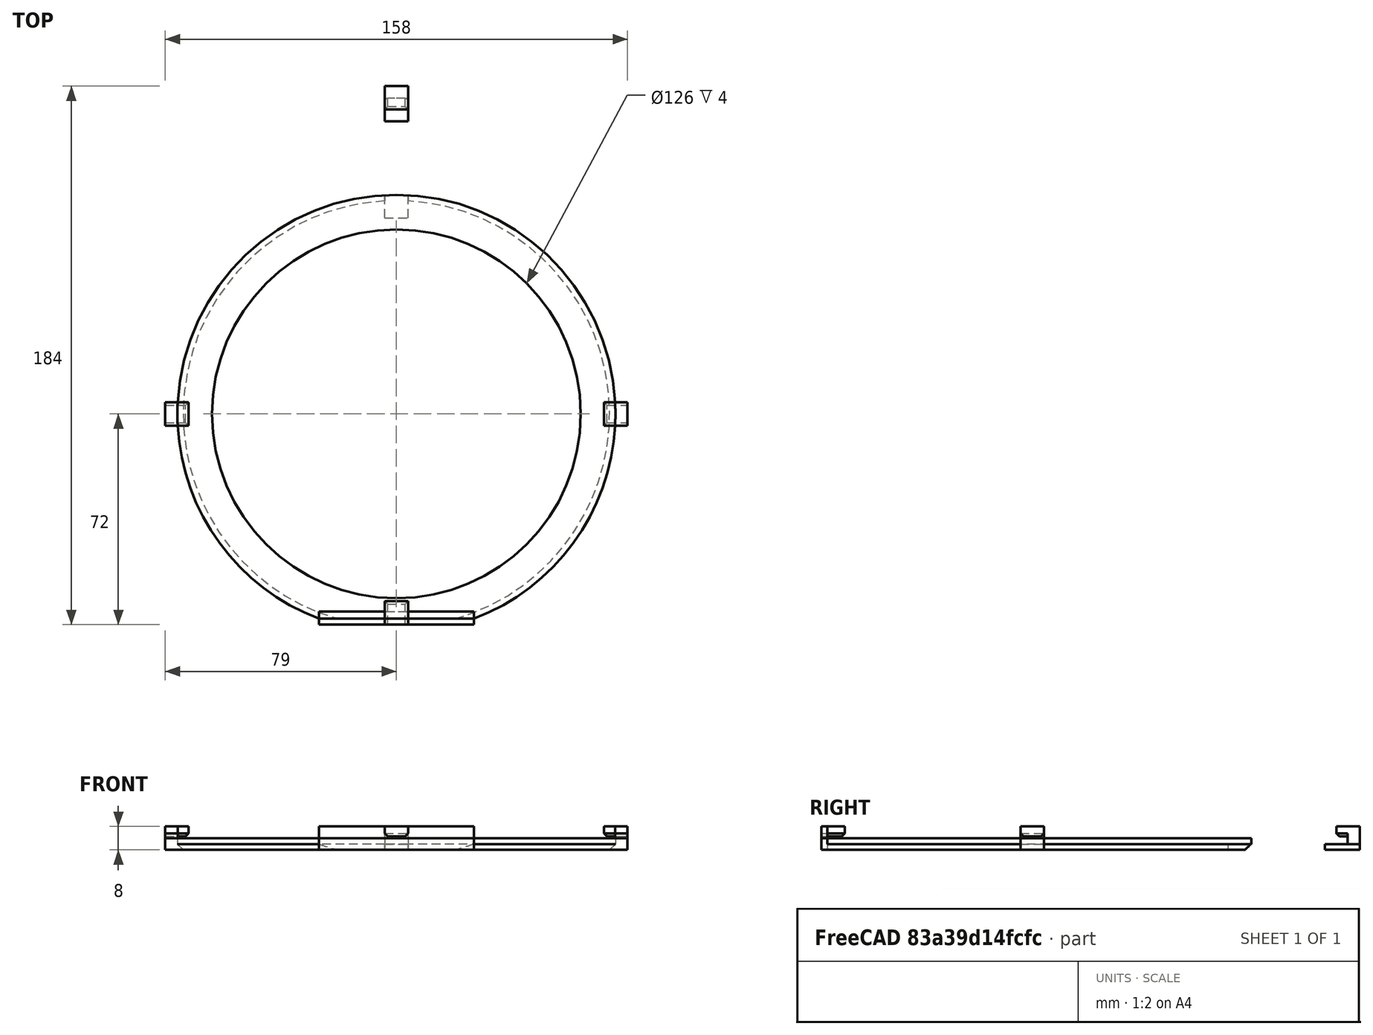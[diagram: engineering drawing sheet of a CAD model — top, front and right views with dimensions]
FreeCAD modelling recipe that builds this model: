
FCSTD DOCUMENT  (FreeCAD 0.19R0.19.2)
Label: waferHolder_009
License: All rights reserved
LicenseURL: http://en.wikipedia.org/wiki/All_rights_reserved
objects: Part::Box×18, Part::Chamfer×14, Part::Cut×8, Sketcher::SketchObject×5, Part::Extrusion×5, Part::MultiFuse×2
note: 52 computed .brp shape members not serialized (recipe doc carries the construction recipe); baked Part::Feature solids carry a one-line shape summary decoded from their .brp

FEATURE [Sketcher::SketchObject] Sketch
  FullyConstrained = true
  sketch-geometry (3):
    g0: Circle CenterX=-3.1415e-12 CenterY=5.6243e-12 CenterZ=0 NormalX=0 NormalY=0 NormalZ=1 AngleXU=0 Radius=63
    g1: ArcOfCircle CenterX=-3.1415e-12 CenterY=5.6243e-12 CenterZ=0 NormalX=0 NormalY=0 NormalZ=1 AngleXU=0 Radius=74.8482 StartAngle=5.07429 EndAngle=10.6337
    g2: LineSegment StartX=-26.5 StartY=-70.0001 StartZ=0 EndX=26.5 EndY=-70.0001 EndZ=0
  constraints (6):
    c: Block(g0)
    c: Coincident(g1,g0)
    c: Block(g1)
    c: Coincident(g2,g1)
    c: Coincident(g2,g1)
    c: Horizontal(g2)
FEATURE [Part::Box] Box  label="holderBitLeft"
  AttacherType = Attacher::AttachEngine3D
  Height = 4
  Length = 8
  Placement = pos=(-79,-4,0) rot=(0,0,1;0rad)
  Width = 8
FEATURE [Part::Box] Box001  label="bitHolderTopCutout"
  AttacherType = Attacher::AttachEngine3D
  Height = 4
  Length = 8
  Placement = pos=(-4,67,-2) rot=(0,0,1;0rad)
  Width = 12
FEATURE [Part::Extrusion] Extrude  label="mainHolderRing"
  Base = -> Sketch
  Dir = (0,0,1)
  DirMode = 2
  FaceMakerClass = Part::FaceMakerBullseye
  LengthFwd = 4
  LengthRev = 0
  Solid = true
  Symmetric = false
FEATURE [Part::Box] Box002  label="holderBitRight"
  AttacherType = Attacher::AttachEngine3D
  Height = 4
  Length = 8
  Placement = pos=(71,-4,0) rot=(0,0,1;0rad)
  Width = 8
FEATURE [Part::Box] Box003  label="bitHolderTop"
  AttacherType = Attacher::AttachEngine3D
  Height = 2
  Length = 8
  Placement = pos=(-4,100,0) rot=(0,0,1;0rad)
  Width = 12
FEATURE [Part::Chamfer] Chamfer
  Base = -> Extrude
  Edges = 1 edges r=2: [Edge3]
FEATURE [Part::Cut] Cut  label="mainHolderRing001"
  Base = -> Chamfer
  Tool = -> Box001
FEATURE [Part::Box] Box004  label="holderBitLeft001"
  AttacherType = Attacher::AttachEngine3D
  Height = 4
  Length = 6
  Placement = pos=(-79,-4,0) rot=(0,0,1;0rad)
  Width = 8
FEATURE [Part::Box] Box005  label="holderBitright002"
  AttacherType = Attacher::AttachEngine3D
  Height = 4
  Length = 6
  Placement = pos=(73,-4,0) rot=(0,0,1;0rad)
  Width = 8
FEATURE [Part::MultiFuse] Fusion  label="holders"
  Shapes = -> [Box004,Box005]
FEATURE [Sketcher::SketchObject] Sketch001
  FullyConstrained = true
  sketch-geometry (3):
    g0: Circle CenterX=-3.1415e-12 CenterY=5.6243e-12 CenterZ=0 NormalX=0 NormalY=0 NormalZ=1 AngleXU=0 Radius=63
    g1: ArcOfCircle CenterX=-3.1415e-12 CenterY=5.6243e-12 CenterZ=0 NormalX=0 NormalY=0 NormalZ=1 AngleXU=0 Radius=74.8482 StartAngle=5.07429 EndAngle=10.6337
    g2: LineSegment StartX=-26.5 StartY=-70.0001 StartZ=0 EndX=26.5 EndY=-70.0001 EndZ=0
  constraints (6):
    c: Block(g0)
    c: Coincident(g1,g0)
    c: Block(g1)
    c: Coincident(g2,g1)
    c: Coincident(g2,g1)
    c: Horizontal(g2)
FEATURE [Part::Extrusion] Extrude001  label="mainHolderRing002"
  Base = -> Sketch001
  Dir = (0,0,1)
  DirMode = 2
  FaceMakerClass = Part::FaceMakerBullseye
  LengthFwd = 4
  LengthRev = 0
  Solid = true
  Symmetric = false
FEATURE [Part::Cut] Cut001  label="leftAndRightHolderBits"
  Base = -> Fusion
  Placement = pos=(0,0,4) rot=(0,0,1;0rad)
  Tool = -> Extrude001
FEATURE [Part::Box] Box006  label="holderBitLeft002"
  AttacherType = Attacher::AttachEngine3D
  Height = 3.4
  Length = 8
  Placement = pos=(-79,-4,4.6) rot=(0,0,1;0rad)
  Width = 8
FEATURE [Part::Box] Box007  label="holderBitRight002"
  AttacherType = Attacher::AttachEngine3D
  Height = 3.4
  Length = 8
  Placement = pos=(71,-4,4.6) rot=(0,0,1;0rad)
  Width = 8
FEATURE [Part::Box] Box008  label="holderBitLeft003"
  AttacherType = Attacher::AttachEngine3D
  Height = 2
  Length = 8
  Placement = pos=(-4,71,2) rot=(0,0,1;0rad)
  Width = 8
FEATURE [Part::Box] Box009  label="bitHolderTopCutout001"
  AttacherType = Attacher::AttachEngine3D
  Height = 4
  Length = 8
  Placement = pos=(-4,67,-2) rot=(0,0,1;0rad)
  Width = 12
FEATURE [Sketcher::SketchObject] Sketch002
  FullyConstrained = true
  sketch-geometry (3):
    g0: Circle CenterX=-3.1415e-12 CenterY=5.6243e-12 CenterZ=0 NormalX=0 NormalY=0 NormalZ=1 AngleXU=0 Radius=63
    g1: ArcOfCircle CenterX=-3.1415e-12 CenterY=5.6243e-12 CenterZ=0 NormalX=0 NormalY=0 NormalZ=1 AngleXU=0 Radius=74.8482 StartAngle=5.07429 EndAngle=10.6337
    g2: LineSegment StartX=-26.5 StartY=-70.0001 StartZ=0 EndX=26.5 EndY=-70.0001 EndZ=0
  constraints (6):
    c: Block(g0)
    c: Coincident(g1,g0)
    c: Block(g1)
    c: Coincident(g2,g1)
    c: Coincident(g2,g1)
    c: Horizontal(g2)
FEATURE [Part::Extrusion] Extrude002  label="mainHolderRing003"
  Base = -> Sketch002
  Dir = (0,0,1)
  DirMode = 2
  FaceMakerClass = Part::FaceMakerBullseye
  LengthFwd = 4
  LengthRev = 0
  Solid = true
  Symmetric = false
FEATURE [Part::Chamfer] Chamfer001
  Base = -> Extrude002
  Edges = 1 edges r=2: [Edge3]
FEATURE [Part::Cut] Cut002  label="mainHolderRing004"
  Base = -> Chamfer001
  Tool = -> Box009
FEATURE [Part::Cut] Cut003  label="bitHolderTop001"
  Base = -> Box008
  Tool = -> Cut002
FEATURE [Part::Box] Box010  label="holderBitLeft004"
  AttacherType = Attacher::AttachEngine3D
  Height = 2
  Length = 8
  Placement = pos=(-4,71,2) rot=(0,0,1;0rad)
  Width = 8
FEATURE [Part::Box] Box011  label="bitHolderTopCutout002"
  AttacherType = Attacher::AttachEngine3D
  Height = 4
  Length = 8
  Placement = pos=(-4,67,-2) rot=(0,0,1;0rad)
  Width = 12
FEATURE [Sketcher::SketchObject] Sketch003
  FullyConstrained = true
  sketch-geometry (3):
    g0: Circle CenterX=-3.1415e-12 CenterY=5.6243e-12 CenterZ=0 NormalX=0 NormalY=0 NormalZ=1 AngleXU=0 Radius=63
    g1: ArcOfCircle CenterX=-3.1415e-12 CenterY=5.6243e-12 CenterZ=0 NormalX=0 NormalY=0 NormalZ=1 AngleXU=0 Radius=74.8482 StartAngle=5.07429 EndAngle=10.6337
    g2: LineSegment StartX=-26.5 StartY=-70.0001 StartZ=0 EndX=26.5 EndY=-70.0001 EndZ=0
  constraints (6):
    c: Block(g0)
    c: Coincident(g1,g0)
    c: Block(g1)
    c: Coincident(g2,g1)
    c: Coincident(g2,g1)
    c: Horizontal(g2)
FEATURE [Part::Extrusion] Extrude003  label="mainHolderRing006"
  Base = -> Sketch003
  Dir = (0,0,1)
  DirMode = 2
  FaceMakerClass = Part::FaceMakerBullseye
  LengthFwd = 4
  LengthRev = 0
  Solid = true
  Symmetric = false
FEATURE [Part::Chamfer] Chamfer002
  Base = -> Extrude003
  Edges = 1 edges r=2: [Edge3]
FEATURE [Part::Cut] Cut005  label="mainHolderRing005"
  Base = -> Chamfer002
  Tool = -> Box011
FEATURE [Part::Cut] Cut004  label="bitHolderTop002"
  Base = -> Box010
  Placement = pos=(0,0,2) rot=(0,0,1;0rad)
  Tool = -> Cut005
FEATURE [Part::Box] Box012  label="holderBitLeft005"
  AttacherType = Attacher::AttachEngine3D
  Height = 2
  Length = 8
  Placement = pos=(-4,71,2) rot=(0,0,1;0rad)
  Width = 8
FEATURE [Part::Box] Box013  label="bitHolderTopCutout003"
  AttacherType = Attacher::AttachEngine3D
  Height = 4
  Length = 8
  Placement = pos=(-4,67,-2) rot=(0,0,1;0rad)
  Width = 12
FEATURE [Sketcher::SketchObject] Sketch004
  FullyConstrained = true
  sketch-geometry (3):
    g0: Circle CenterX=-3.1415e-12 CenterY=5.6243e-12 CenterZ=0 NormalX=0 NormalY=0 NormalZ=1 AngleXU=0 Radius=63
    g1: ArcOfCircle CenterX=-3.1415e-12 CenterY=5.6243e-12 CenterZ=0 NormalX=0 NormalY=0 NormalZ=1 AngleXU=0 Radius=74.8482 StartAngle=5.07429 EndAngle=10.6337
    g2: LineSegment StartX=-26.5 StartY=-70.0001 StartZ=0 EndX=26.5 EndY=-70.0001 EndZ=0
  constraints (6):
    c: Block(g0)
    c: Coincident(g1,g0)
    c: Block(g1)
    c: Coincident(g2,g1)
    c: Coincident(g2,g1)
    c: Horizontal(g2)
FEATURE [Part::Extrusion] Extrude004  label="mainHolderRing008"
  Base = -> Sketch004
  Dir = (0,0,1)
  DirMode = 2
  FaceMakerClass = Part::FaceMakerBullseye
  LengthFwd = 4
  LengthRev = 0
  Solid = true
  Symmetric = false
FEATURE [Part::Chamfer] Chamfer003
  Base = -> Extrude004
  Edges = 1 edges r=2: [Edge3]
FEATURE [Part::Cut] Cut007  label="mainHolderRing007"
  Base = -> Chamfer003
  Tool = -> Box013
FEATURE [Part::Cut] Cut006  label="bitHolderTop003"
  Base = -> Box012
  Placement = pos=(0,0,4) rot=(0,0,1;0rad)
  Tool = -> Cut007
FEATURE [Part::Box] Box014  label="bitHoldertop006"
  AttacherType = Attacher::AttachEngine3D
  Height = 3.4
  Length = 8
  Placement = pos=(-4,71,4.6) rot=(0,0,1;0rad)
  Width = 8
FEATURE [Part::MultiFuse] Fusion001  label="holderTop"
  Placement = pos=(0,33,0) rot=(0,0,1;0rad)
  Shapes = -> [Cut003,Cut004,Cut006,Box014]
FEATURE [Part::Chamfer] Chamfer004
  Base = -> Fusion001
  Edges = 1 edges r=1: [Edge16]
FEATURE [Part::Chamfer] Chamfer005
  Base = -> Box006
  Edges = 1 edges r=1: [Edge8]
FEATURE [Part::Chamfer] Chamfer006
  Base = -> Box007
  Edges = 1 edges r=1: [Edge4]
FEATURE [Part::Chamfer] Chamfer007
  Base = -> Chamfer006
  Edges = 1 edges r=1: [Edge13]
FEATURE [Part::Chamfer] Chamfer008
  Base = -> Chamfer007
  Edges = 1 edges r=1: [Edge5]
FEATURE [Part::Chamfer] Chamfer009
  Base = -> Chamfer004
  Edges = 1 edges r=1: [Edge1]
FEATURE [Part::Chamfer] Chamfer010
  Base = -> Chamfer009
  Edges = 1 edges r=1: [Edge32]
FEATURE [Part::Chamfer] Chamfer011
  Base = -> Chamfer005
  Edges = 1 edges r=1: [Edge5]
FEATURE [Part::Chamfer] Chamfer012
  Base = -> Chamfer011
  Edges = 1 edges r=1: [Edge16]
FEATURE [Part::Box] Box015  label="holderBottom"
  AttacherType = Attacher::AttachEngine3D
  Height = 4
  Length = 53
  Placement = pos=(-26.5,-72,0) rot=(0,0,1;0rad)
  Width = 4.5
FEATURE [Part::Box] Box016  label="holderBottom001"
  AttacherType = Attacher::AttachEngine3D
  Height = 4
  Length = 53
  Placement = pos=(-26.5,-72,4) rot=(0,0,1;0rad)
  Width = 2
FEATURE [Part::Box] Box017  label="holderBottom002"
  AttacherType = Attacher::AttachEngine3D
  Height = 3.4
  Length = 8
  Placement = pos=(-4,-72,4.6) rot=(0,0,1;0rad)
  Width = 8
FEATURE [Part::Chamfer] Chamfer013  label="holderBottom003"
  Base = -> Box017
  Edges = 3 edges r=1: [Edge4,Edge8,Edge11]
